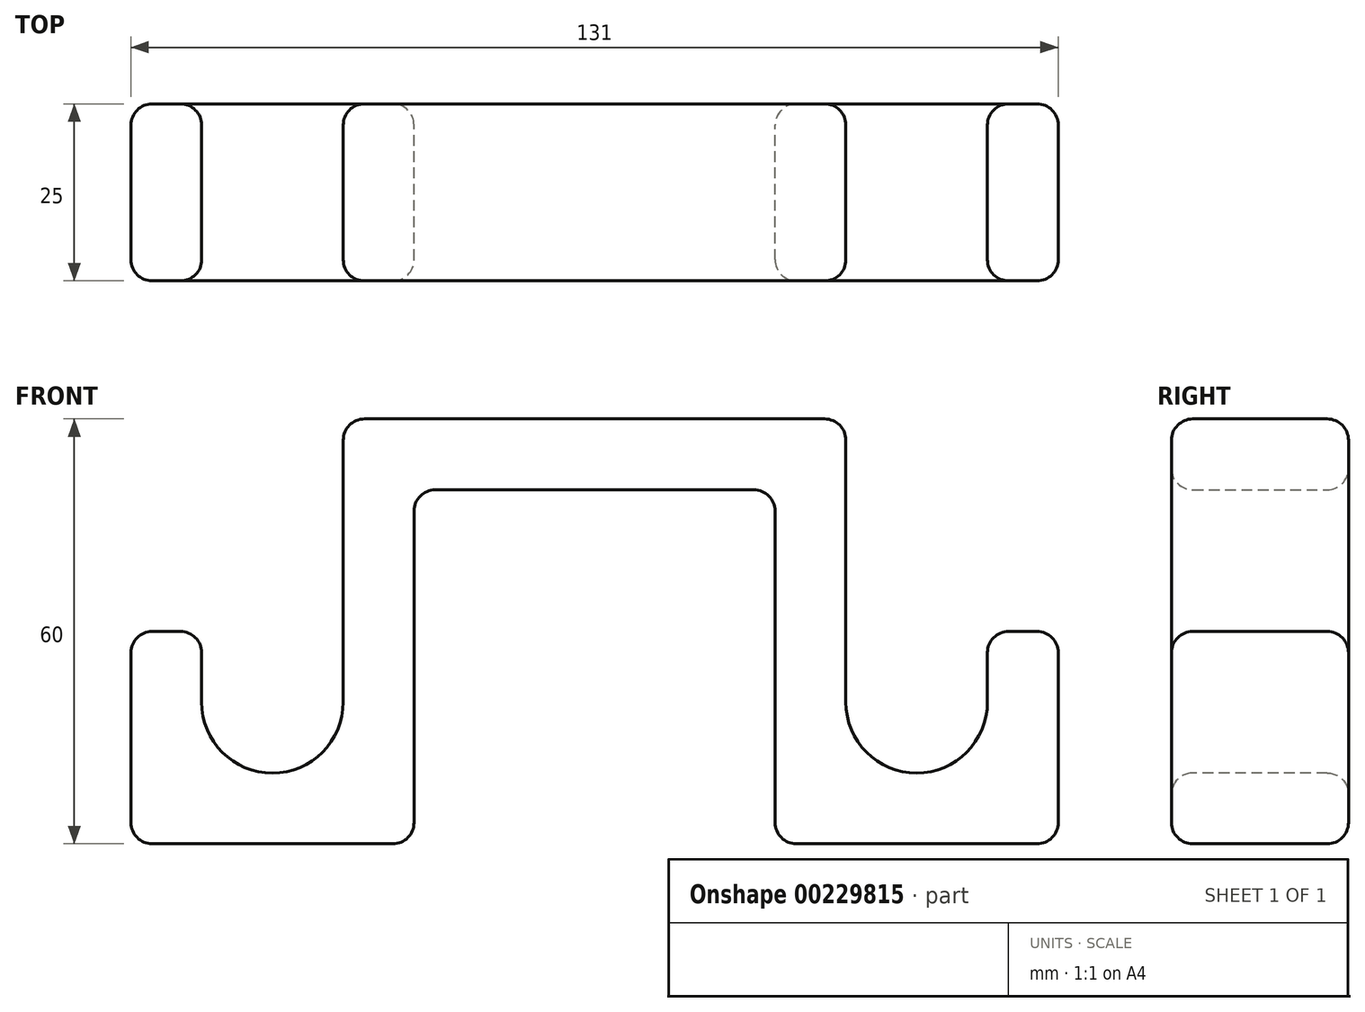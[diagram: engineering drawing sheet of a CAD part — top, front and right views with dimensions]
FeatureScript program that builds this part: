
annotation { "Feature Type Name" : "Feature", "Feature Type Description" : "" }
export const myFeature = defineFeature(function(context is Context, id is Id, definition is map)
    precondition{}
    {
        {
            var Q0;
            Q0=qCreatedBy(makeId("Front.planeOp"),FACE);
            var sketch = newSketch(context, id + "F0", { "sketchPlane" : qUnion([Q0])});
            skLineSegment(sketch, "E0", {"start": v(0, 0) * mm, "end": v(0, 60) * mm});
            skLineSegment(sketch, "E1", {"start": v(0, 60) * mm, "end": v(-71, 60) * mm});
            skLineSegment(sketch, "E2", {"start": v(-71, 60) * mm, "end": v(-71, 10) * mm});
            skLineSegment(sketch, "E3", {"start": v(-71, 10) * mm, "end": v(-91, 10) * mm});
            skLineSegment(sketch, "E4", {"start": v(-91, 10) * mm, "end": v(-91, 30) * mm});
            skLineSegment(sketch, "E5", {"start": v(-91, 30) * mm, "end": v(-101, 30) * mm});
            skLineSegment(sketch, "E6", {"start": v(-101, 30) * mm, "end": v(-101, 0) * mm});
            skLineSegment(sketch, "E7", {"start": v(-101, 0) * mm, "end": v(-61, 0) * mm});
            skLineSegment(sketch, "E8", {"start": v(-61, 0) * mm, "end": v(-61, 50) * mm});
            skLineSegment(sketch, "E9", {"start": v(-61, 50) * mm, "end": v(-10, 50) * mm});
            skLineSegment(sketch, "E10", {"start": v(-10, 50) * mm, "end": v(-10, 0) * mm});
            skLineSegment(sketch, "E11", {"start": v(-10, 0) * mm, "end": v(0, 0) * mm});
            skSolve(sketch);
        }
        {
            var Q0;
            Q0 = qSketchRegion(id + "F0", true);
            extrude(context, id + "F1", {"entities" : qUnion([Q0]), "depth" : 25 * mm});
        }
        {
            var Q0;
            Q0=makeQuery(id+"F1.opExtrude","SWEPT_EDGE",EDGE,{"disambiguationData":[OSD([sQuery(id+"F0.wireOp",EDGE,"E1"),sQuery(id+"F0.wireOp",EDGE,"E2")])]});
            var Q1;
            Q1=makeQuery(id+"F1.opExtrude","SWEPT_EDGE",EDGE,{"disambiguationData":[OSD([sQuery(id+"F0.wireOp",EDGE,"E0"),sQuery(id+"F0.wireOp",EDGE,"E1")])]});
            var Q2;
            Q2=makeQuery(id+"F1.opExtrude","SWEPT_EDGE",EDGE,{"disambiguationData":[OSD([sQuery(id+"F0.wireOp",EDGE,"E9"),sQuery(id+"F0.wireOp",EDGE,"E10")])]});
            var Q3;
            Q3=makeQuery(id+"F1.opExtrude","SWEPT_EDGE",EDGE,{"disambiguationData":[OSD([sQuery(id+"F0.wireOp",EDGE,"E8"),sQuery(id+"F0.wireOp",EDGE,"E9")])]});
            var Q4;
            Q4=makeQuery(id+"F1.opExtrude","SWEPT_EDGE",EDGE,{"disambiguationData":[OSD([sQuery(id+"F0.wireOp",EDGE,"E7"),sQuery(id+"F0.wireOp",EDGE,"E8")])]});
            var Q5;
            Q5=makeQuery(id+"F1.opExtrude","SWEPT_EDGE",EDGE,{"disambiguationData":[OSD([sQuery(id+"F0.wireOp",EDGE,"E10"),sQuery(id+"F0.wireOp",EDGE,"E11")])]});
            var Q6;
            Q6=makeQuery(id+"F1.opExtrude","SWEPT_EDGE",EDGE,{"disambiguationData":[OSD([sQuery(id+"F0.wireOp",EDGE,"E0"),sQuery(id+"F0.wireOp",EDGE,"E11")])]});
            var Q7;
            Q7=makeQuery(id+"F1.opExtrude","SWEPT_EDGE",EDGE,{"disambiguationData":[OSD([sQuery(id+"F0.wireOp",EDGE,"E6"),sQuery(id+"F0.wireOp",EDGE,"E7")])]});
            var Q8;
            Q8=makeQuery(id+"F1.opExtrude","SWEPT_EDGE",EDGE,{"disambiguationData":[OSD([sQuery(id+"F0.wireOp",EDGE,"E5"),sQuery(id+"F0.wireOp",EDGE,"E6")])]});
            var Q9;
            Q9=makeQuery(id+"F1.opExtrude","SWEPT_EDGE",EDGE,{"disambiguationData":[OSD([sQuery(id+"F0.wireOp",EDGE,"E4"),sQuery(id+"F0.wireOp",EDGE,"E5")])]});
            fillet(context, id + "F2", {"entities" : qUnion([Q0, Q1, Q2, Q3, Q4, Q5, Q6, Q7, Q8, Q9]), "radius" : 3 * mm, "tangentPropagation" : true, "allowEdgeOverflow" : false});
        }
        {
            var Q0;
            Q0=makeQuery(id+"F1.opExtrude","SWEPT_EDGE",EDGE,{"disambiguationData":[OSD([sQuery(id+"F0.wireOp",EDGE,"E3"),sQuery(id+"F0.wireOp",EDGE,"E4")])]});
            var Q1;
            Q1=makeQuery(id+"F1.opExtrude","SWEPT_EDGE",EDGE,{"disambiguationData":[OSD([sQuery(id+"F0.wireOp",EDGE,"E2"),sQuery(id+"F0.wireOp",EDGE,"E3")])]});
            fillet(context, id + "F3", {"entities" : qUnion([Q0, Q1]), "radius" : 10 * mm, "tangentPropagation" : true, "allowEdgeOverflow" : false});
        }
        {
            var Q0;
            Q0=makeQuery(id+"F1.opExtrude","SWEPT_FACE",FACE,{"disambiguationData":[OSD([sQuery(id+"F0.wireOp",EDGE,"E0")])]});
            var Q1;
            Q1=makeQuery(id+"F1.opExtrude","SWEPT_FACE",FACE,{"disambiguationData":[OSD([sQuery(id+"F0.wireOp",EDGE,"E2")])]});
            cPlane(context, id + "F4", {"entities" : qUnion([Q0, Q1]), "cplaneType" : CPlaneType.MID_PLANE, "offset" : 25 * mm, "width" : 150 * mm, "height" : 150 * mm});
        }
        {
            var Q0;
            Q0=makeQuery(id+"F1.opExtrude","CAP_FACE",FACE,{"disambiguationData":[OSD([sQuery(id+"F0.wireOp",EDGE,"E0"),sQuery(id+"F0.wireOp",EDGE,"E1"),sQuery(id+"F0.wireOp",EDGE,"E2"),sQuery(id+"F0.wireOp",EDGE,"E3"),sQuery(id+"F0.wireOp",EDGE,"E4"),sQuery(id+"F0.wireOp",EDGE,"E5"),sQuery(id+"F0.wireOp",EDGE,"E6"),sQuery(id+"F0.wireOp",EDGE,"E7"),sQuery(id+"F0.wireOp",EDGE,"E8"),sQuery(id+"F0.wireOp",EDGE,"E9"),sQuery(id+"F0.wireOp",EDGE,"E10"),sQuery(id+"F0.wireOp",EDGE,"E11")])],"isStart":false});
            var Q1;
            Q1=makeQuery(id+"F1.opExtrude","CAP_FACE",FACE,{"disambiguationData":[OSD([sQuery(id+"F0.wireOp",EDGE,"E0"),sQuery(id+"F0.wireOp",EDGE,"E1"),sQuery(id+"F0.wireOp",EDGE,"E2"),sQuery(id+"F0.wireOp",EDGE,"E3"),sQuery(id+"F0.wireOp",EDGE,"E4"),sQuery(id+"F0.wireOp",EDGE,"E5"),sQuery(id+"F0.wireOp",EDGE,"E6"),sQuery(id+"F0.wireOp",EDGE,"E7"),sQuery(id+"F0.wireOp",EDGE,"E8"),sQuery(id+"F0.wireOp",EDGE,"E9"),sQuery(id+"F0.wireOp",EDGE,"E10"),sQuery(id+"F0.wireOp",EDGE,"E11")])],"isStart":true});
            fillet(context, id + "F5", {"entities" : qUnion([Q0, Q1]), "radius" : 3 * mm, "tangentPropagation" : true, "allowEdgeOverflow" : false});
        }
        {
            var Q0;
            Q0=makeQuery(id+"F1.opExtrude","SWEPT_BODY",BODY,{"disambiguationData":[OSD([sQuery(id+"F0.wireOp",EDGE,"E0"),sQuery(id+"F0.wireOp",EDGE,"E1"),sQuery(id+"F0.wireOp",EDGE,"E2"),sQuery(id+"F0.wireOp",EDGE,"E3"),sQuery(id+"F0.wireOp",EDGE,"E4"),sQuery(id+"F0.wireOp",EDGE,"E5"),sQuery(id+"F0.wireOp",EDGE,"E6"),sQuery(id+"F0.wireOp",EDGE,"E7"),sQuery(id+"F0.wireOp",EDGE,"E8"),sQuery(id+"F0.wireOp",EDGE,"E9"),sQuery(id+"F0.wireOp",EDGE,"E10"),sQuery(id+"F0.wireOp",EDGE,"E11")])]});
            var Q1;
            Q1=qCreatedBy(id+"F4.planeOp",FACE);
            mirror(context, id + "F6", {"operationType" : NewBodyOperationType.ADD, "entities" : qUnion([Q0]), "mirrorPlane" : qUnion([Q1])});
        }
    });
